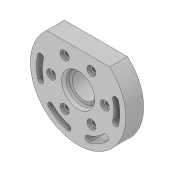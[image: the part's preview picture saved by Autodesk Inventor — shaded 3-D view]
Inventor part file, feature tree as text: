
AUTODESK INVENTOR PART (.ipt)
format: ipt  version: 2017 (Build 210142000, 142)  size: 183,296 bytes
history: native  units: in
note: dims shown in document units (in); Inventor stores cm internally (conversion verified against a paired STEP export)
features: sketch x3, extrude x2, hole x2, pattern_circular x1, chamfer x1
ambient origin geometry x8: Origin, YZ Plane, XZ Plane, XY Plane, X Axis, Y Axis, Z Axis, Center Point
bodies: Solid1 (feature_tree)
feature tree (9):
  extrude  "Extrusion1"  Depth=0.63in
  extrude  "Extrusion2"  Depth=0.512in
  hole  "Hole1"  [1 undecoded]
  hole  "Hole2"  [1 undecoded]
  pattern_circular  "Circular Pattern1"  [2 undecoded]
  chamfer  "Chamfer1"  Distance=0.078in
  sketch  "Sketch1"  dims[d0=1.102in d1=0.63in]
  sketch  "Sketch2"  dims[d2=30.0deg d3=0.512in]
  sketch  "Sketch3"  dims[d4=0.039in d5=1.5748in d7=180.0deg d9=0.236in d10=0.0in d11=0.472in d12=0.078in d13=0.0in d14=1.0in d15=1.0in d16=0.315in d17=0.75in d18=0.393in d19=0.078in d20=0.5635in d21=1.0in d22=0.8108in d23=0.354in d24=0.056in d25=0.146in d26=0.118in d27=0.039in d28=0.5635in d29=0.224in d30=0.8108in d31=2.3622in d32=360.0deg d34=0.039in d35=0.125in d36=30.0deg]
note: 4 required parameter values undecoded (feature->parameter linkage not recoverable at this tier; creation-order binding heuristic only, values carry confidence <= 0.55)
